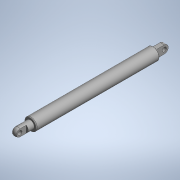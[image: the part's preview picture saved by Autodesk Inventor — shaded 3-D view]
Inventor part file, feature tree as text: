
AUTODESK INVENTOR PART (.ipt)
format: ipt  version: 2020 (Build 240168000, 168)  size: 104,448 bytes
history: native  units: mm (DEFAULTED — no unit token found)
features: other x1, extrude x1
ambient origin geometry x8: Origin, YZ Plane, XZ Plane, XY Plane, X Axis, Y Axis, Z Axis, Center Point
bodies: Solid1 (feature_tree), Solid2 (feature_tree)
feature tree (2):
  other  "LPattern1"
  extrude  "Extrude2"  [1 undecoded]
note: 1 required parameter value undecoded (feature->parameter linkage not recoverable at this tier; creation-order binding heuristic only, values carry confidence <= 0.55)
